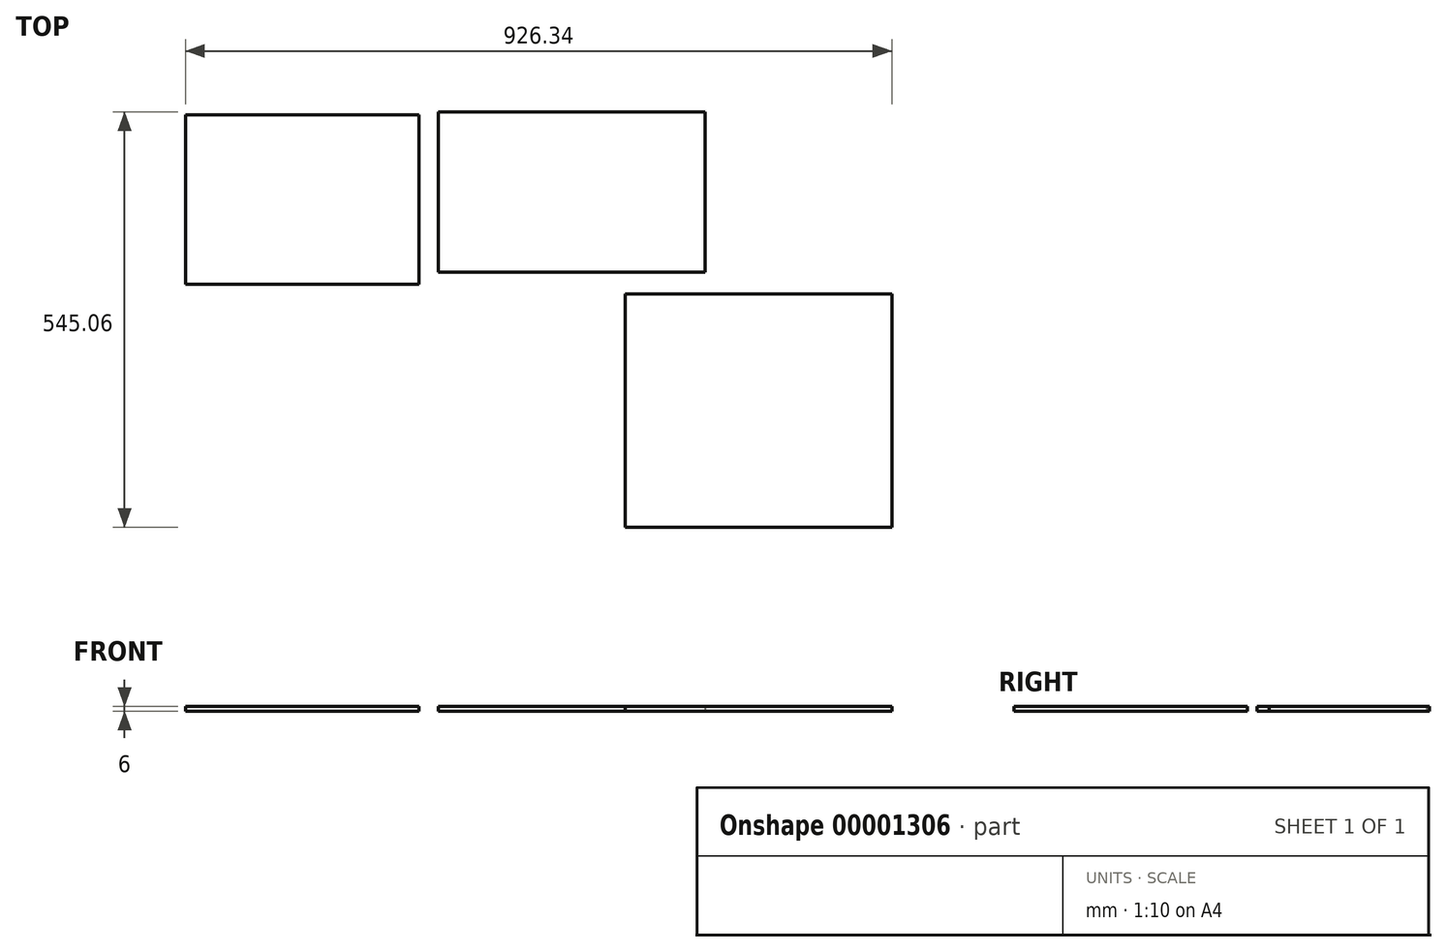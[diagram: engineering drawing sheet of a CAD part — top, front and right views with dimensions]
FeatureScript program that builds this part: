
annotation { "Feature Type Name" : "Feature", "Feature Type Description" : "" }
export const myFeature = defineFeature(function(context is Context, id is Id, definition is map)
    precondition{}
    {
        {
            var Q0;
            Q0=qCreatedBy(makeId("Top.planeOp"),FACE);
            var sketch = newSketch(context, id + "F0", { "sketchPlane" : qUnion([Q0])});
            skLineSegment(sketch, "E0.bottom", {"start": v(-175, -105) * mm, "end": v(175, -105) * mm});
            skLineSegment(sketch, "E0.top", {"start": v(-175, 105) * mm, "end": v(175, 105) * mm});
            skLineSegment(sketch, "E0.left", {"start": v(-175, -105) * mm, "end": v(-175, 105) * mm});
            skLineSegment(sketch, "E0.right", {"start": v(175, -105) * mm, "end": v(175, 105) * mm});
            skPoint(sketch, "E0.middle", {"position": v(0, 0) * mm});
            skSolve(sketch);
        }
        {
            var Q0;
            Q0=makeQuery(id+"F0.imprint","IMPRINT",FACE,{"disambiguationData":[TD([[makeQuery(id+"F0.imprint","IMPRINT",EDGE,{"derivedFrom":sQuery(id+"F0.wireOp",EDGE,"E0.bottom")}),1.0]])]});
            extrude(context, id + "F1", {"entities" : qUnion([Q0]), "depth" : 6 * mm, "offsetDistance" : 25 * mm});
        }
        {
            var Q0;
            Q0=qCreatedBy(makeId("Top.planeOp"),FACE);
            var sketch = newSketch(context, id + "F2", { "sketchPlane" : qUnion([Q0])});
            skLineSegment(sketch, "E1.bottom", {"start": v(69.7, -134.06) * mm, "end": v(419.7, -134.06) * mm});
            skLineSegment(sketch, "E1.top", {"start": v(69.7, -440.06) * mm, "end": v(419.7, -440.06) * mm});
            skLineSegment(sketch, "E1.left", {"start": v(69.7, -134.06) * mm, "end": v(69.7, -440.06) * mm});
            skLineSegment(sketch, "E1.right", {"start": v(419.7, -134.06) * mm, "end": v(419.7, -440.06) * mm});
            skSolve(sketch);
        }
        {
            var Q0;
            Q0=makeQuery(id+"F2.imprint","IMPRINT",FACE,{"disambiguationData":[TD([[makeQuery(id+"F2.imprint","IMPRINT",EDGE,{"derivedFrom":sQuery(id+"F2.wireOp",EDGE,"E1.bottom")}),-1.0]])]});
            extrude(context, id + "F3", {"entities" : qUnion([Q0]), "depth" : 6 * mm, "offsetDistance" : 25 * mm});
        }
        {
            var Q0;
            Q0=qCreatedBy(makeId("Top.planeOp"),FACE);
            var sketch = newSketch(context, id + "F4", { "sketchPlane" : qUnion([Q0])});
            skLineSegment(sketch, "E2.bottom", {"start": v(-506.65, 101.08) * mm, "end": v(-200.65, 101.08) * mm});
            skLineSegment(sketch, "E2.top", {"start": v(-506.65, -120.92) * mm, "end": v(-200.65, -120.92) * mm});
            skLineSegment(sketch, "E2.left", {"start": v(-506.65, 101.08) * mm, "end": v(-506.65, -120.92) * mm});
            skLineSegment(sketch, "E2.right", {"start": v(-200.65, 101.08) * mm, "end": v(-200.65, -120.92) * mm});
            skSolve(sketch);
        }
        {
            var Q0;
            Q0=makeQuery(id+"F4.imprint","IMPRINT",FACE,{"disambiguationData":[TD([[makeQuery(id+"F4.imprint","IMPRINT",EDGE,{"derivedFrom":sQuery(id+"F4.wireOp",EDGE,"E2.bottom")}),-1.0]])]});
            extrude(context, id + "F5", {"entities" : qUnion([Q0]), "depth" : 6 * mm, "offsetDistance" : 25 * mm});
        }
    });
